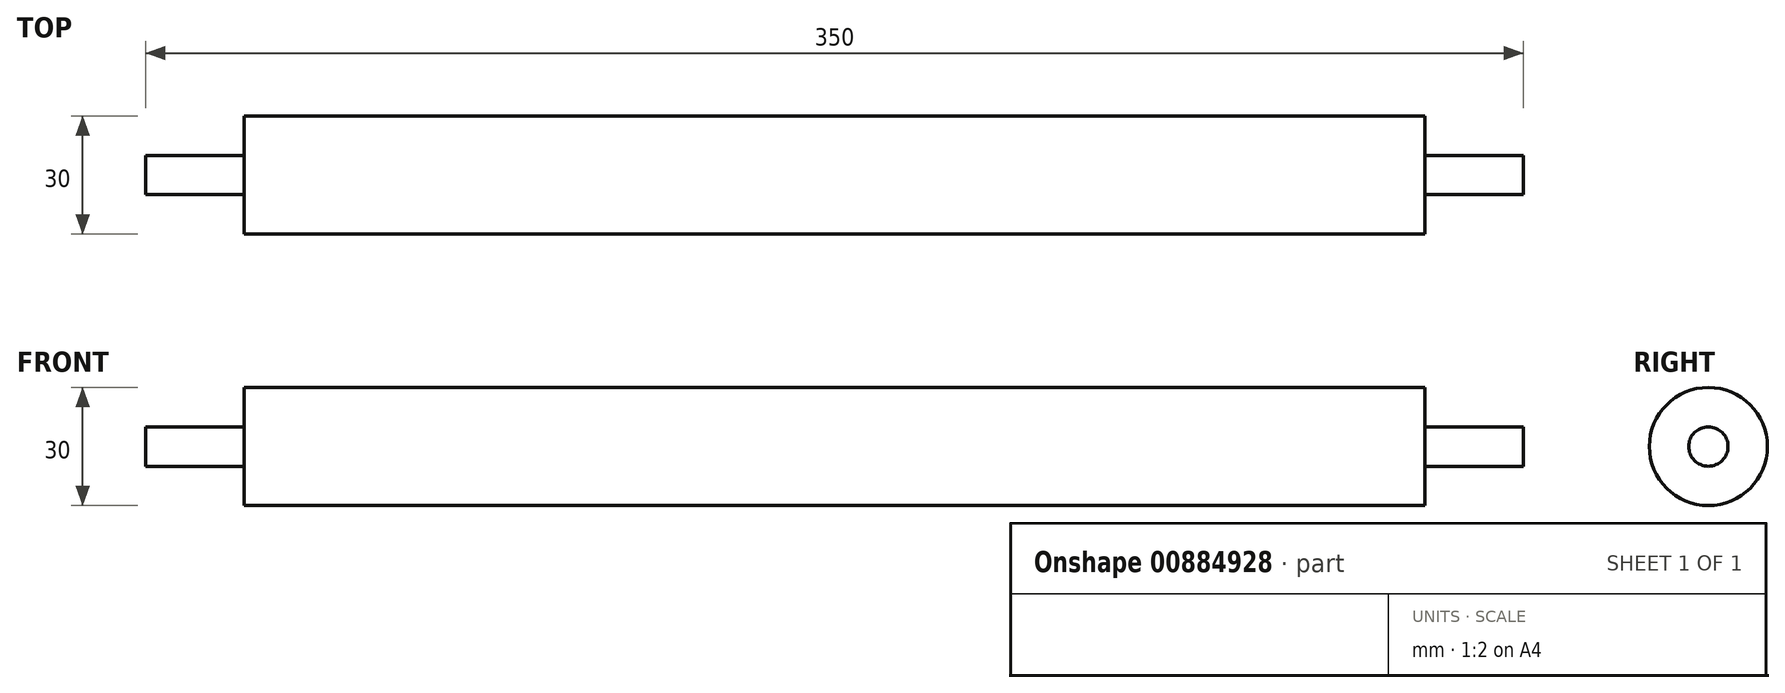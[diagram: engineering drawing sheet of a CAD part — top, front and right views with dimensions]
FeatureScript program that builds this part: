
annotation { "Feature Type Name" : "Feature", "Feature Type Description" : "" }
export const myFeature = defineFeature(function(context is Context, id is Id, definition is map)
    precondition{}
    {
        {
            var Q0;
            Q0=qCreatedBy(makeId("Right.planeOp"),FACE);
            var sketch = newSketch(context, id + "F0", { "sketchPlane" : qUnion([Q0])});
            skCircle(sketch, "E0", {"center": v(0, 0) * mm, "radius": 15 * mm});
            skSolve(sketch);
        }
        {
            var Q0;
            Q0=makeQuery(id+"F0.imprint","IMPRINT",FACE,{"disambiguationData":[TD([[makeQuery(id+"F0.imprint","IMPRINT",EDGE,{"derivedFrom":sQuery(id+"F0.wireOp",EDGE,"E0")}),1.0]])]});
            extrude(context, id + "F1", {"entities" : qUnion([Q0]), "depth" : 300 * mm, "offsetDistance" : 25 * mm});
        }
        {
            var Q0;
            Q0=makeQuery(id+"F1.opExtrude","CAP_FACE",FACE,{"disambiguationData":[OSD([sQuery(id+"F0.wireOp",EDGE,"E0")])],"isStart":false});
            var sketch = newSketch(context, id + "F2", { "sketchPlane" : qUnion([Q0])});
            skCircle(sketch, "E1", {"center": v(0, 0) * mm, "radius": 5 * mm});
            skSolve(sketch);
        }
        {
            var Q0;
            Q0 = qSketchRegion(id + "F2", true);
            extrude(context, id + "F3", {"entities" : qUnion([Q0]), "operationType" : NewBodyOperationType.ADD, "depth" : 25 * mm, "offsetDistance" : 25 * mm});
        }
        {
            var Q0;
            Q0=makeQuery(id+"F1.opExtrude","CAP_FACE",FACE,{"disambiguationData":[OSD([sQuery(id+"F0.wireOp",EDGE,"E0")])],"isStart":true});
            var sketch = newSketch(context, id + "F4", { "sketchPlane" : qUnion([Q0])});
            skCircle(sketch, "E2", {"center": v(0, 0) * mm, "radius": 5 * mm});
            skSolve(sketch);
        }
        {
            var Q0;
            Q0 = qSketchRegion(id + "F4", true);
            extrude(context, id + "F5", {"entities" : qUnion([Q0]), "operationType" : NewBodyOperationType.ADD, "depth" : 25 * mm, "offsetDistance" : 25 * mm});
        }
    });
